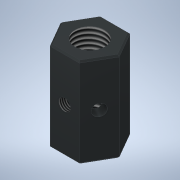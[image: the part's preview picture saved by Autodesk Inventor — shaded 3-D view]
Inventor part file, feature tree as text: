
AUTODESK INVENTOR PART (.ipt)
format: ipt  version: 2020 (Build 240168000, 168)  size: 163,840 bytes
history: native  units: mm
features: thread x4, extrude x3, sketch x3, chamfer x1, mirror x1
ambient origin geometry x8: Origin, YZ Plane, XZ Plane, XY Plane, X Axis, Y Axis, Z Axis, Center Point
bodies: Solid1 (feature_tree)
feature tree (12):
  extrude  "Extrusion1"  Depth=2.0mm
  chamfer  "Chamfer1"  Distance=30.0mm
  thread  "Thread1"  [1 undecoded]
  extrude  "Extrusion2"  Depth=10.0mm
  thread  "Thread2"  [1 undecoded]
  thread  "Thread3"  [1 undecoded]
  extrude  "Выдавливание3"  Depth=10.0mm TaperAngle=0.0deg
  thread  "Резьба4"
  mirror  "Зеркальное отражение1"
  sketch  "Sketch1"  dims[d0=10.0mm d1=17.0mm d2=30.0mm d3=0.0mm d4=0.5mm d5=2.0mm d6=45.0deg]
  sketch  "Sketch2"  dims[d7=10.0mm d8=0.0mm d9=4.0mm d10=15.0mm d11=26.75mm d12=0.0mm d13=10.0mm d14=0.0mm d15=10.0mm d16=0.0mm d17=4.0mm d18=5.25mm d19=0.0mm d20=3.917mm d21=0.0mm]
  sketch  "Эскиз3"
note: 3 required parameter values undecoded (feature->parameter linkage not recoverable at this tier; creation-order binding heuristic only, values carry confidence <= 0.55)
